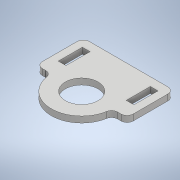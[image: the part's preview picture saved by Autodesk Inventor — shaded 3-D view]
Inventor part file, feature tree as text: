
AUTODESK INVENTOR PART (.ipt)
format: ipt  version: 2020 (Build 240168000, 168)  size: 130,048 bytes
history: native  units: mm
features: other x1, extrude x1, sketch x1
ambient origin geometry x8: Origin, YZ Plane, XZ Plane, XY Plane, X Axis, Y Axis, Z Axis, Center Point
bodies: Body1 (feature_tree)
feature tree (3):
  other  "Твердое тело1"
  extrude  "Выдавливание1"  Depth=5.0mm TaperAngle=0.0deg
  sketch  "Эскиз1"
